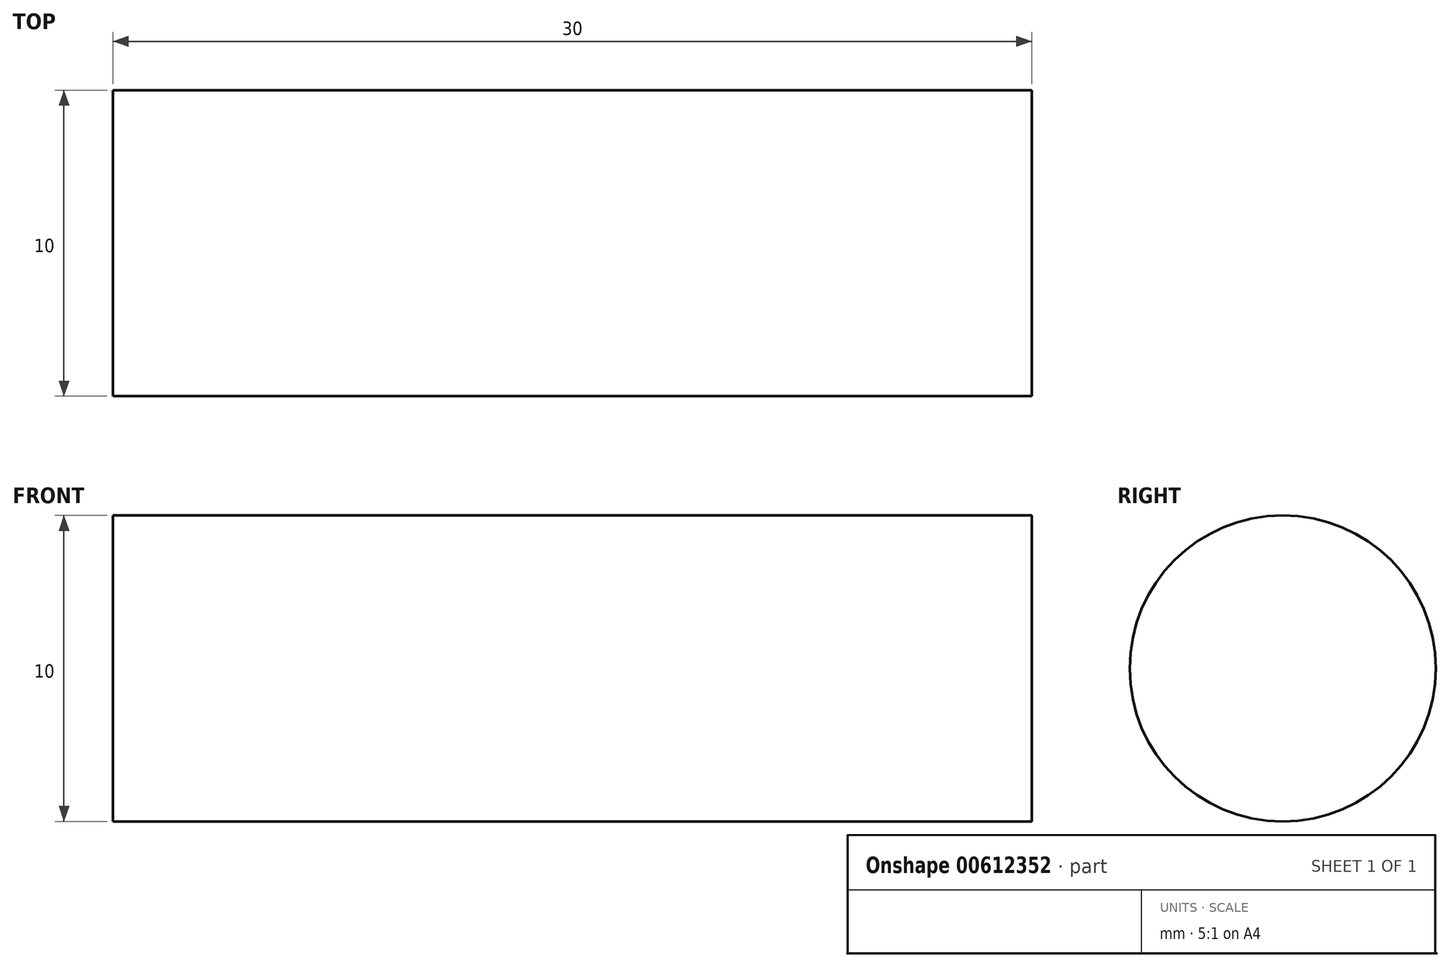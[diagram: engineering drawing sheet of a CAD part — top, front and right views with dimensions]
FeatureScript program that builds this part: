
annotation { "Feature Type Name" : "Feature", "Feature Type Description" : "" }
export const myFeature = defineFeature(function(context is Context, id is Id, definition is map)
    precondition{}
    {
        {
            var Q0;
            Q0=qCreatedBy(makeId("Right.planeOp"),FACE);
            var sketch = newSketch(context, id + "F0", { "sketchPlane" : qUnion([Q0])});
            skCircle(sketch, "E0", {"center": v(0, 0) * mm, "radius": 5 * mm});
            skSolve(sketch);
        }
        {
            var Q0;
            Q0=makeQuery(id+"F0.imprint","IMPRINT",FACE,{"disambiguationData":[TD([[makeQuery(id+"F0.imprint","IMPRINT",EDGE,{"derivedFrom":sQuery(id+"F0.wireOp",EDGE,"E0")}),1.0]])]});
            extrude(context, id + "F1", {"entities" : qUnion([Q0]), "depth" : 30 * mm, "offsetDistance" : 25 * mm});
        }
    });
